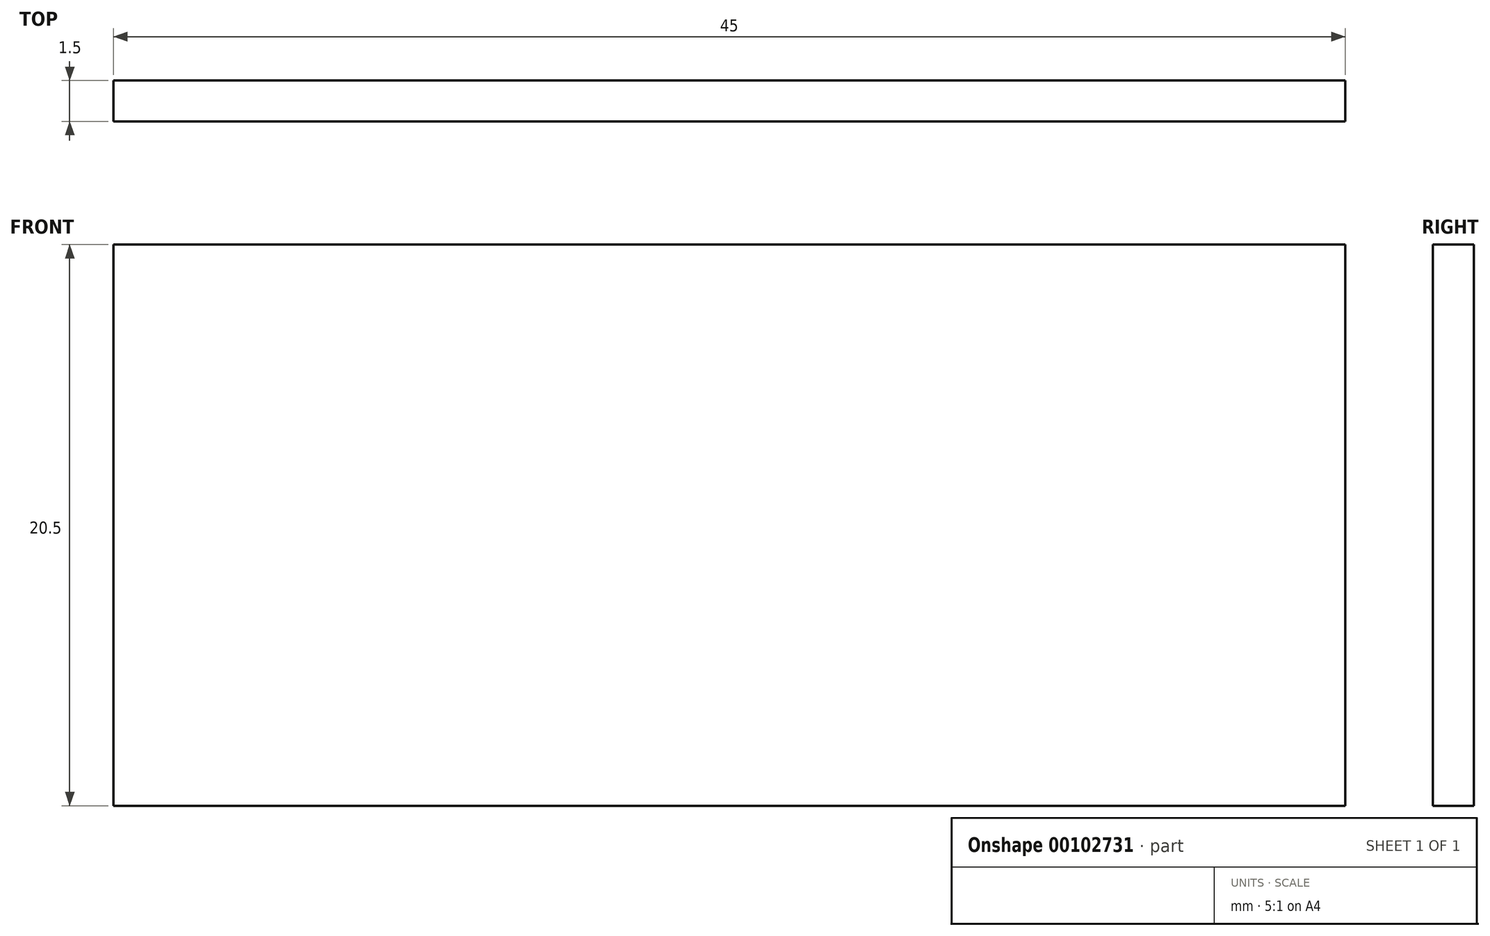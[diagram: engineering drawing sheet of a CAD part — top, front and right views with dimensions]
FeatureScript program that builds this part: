
annotation { "Feature Type Name" : "Feature", "Feature Type Description" : "" }
export const myFeature = defineFeature(function(context is Context, id is Id, definition is map)
    precondition{}
    {
        {
            var Q0;
            Q0=qCreatedBy(makeId("Front.planeOp"),FACE);
            var sketch = newSketch(context, id + "F0", { "sketchPlane" : qUnion([Q0])});
            skLineSegment(sketch, "E0.bottom", {"start": v(22.5, 10.25) * mm, "end": v(-22.5, 10.25) * mm});
            skLineSegment(sketch, "E0.top", {"start": v(22.5, -10.25) * mm, "end": v(-22.5, -10.25) * mm});
            skLineSegment(sketch, "E0.left", {"start": v(22.5, 10.25) * mm, "end": v(22.5, -10.25) * mm});
            skLineSegment(sketch, "E0.right", {"start": v(-22.5, 10.25) * mm, "end": v(-22.5, -10.25) * mm});
            skPoint(sketch, "E0.middle", {"position": v(0, 0) * mm});
            skPoint(sketch, "E1", {"position": v(-13, 0) * mm});
            skPoint(sketch, "E2", {"position": v(13, 0) * mm});
            skPoint(sketch, "E3", {"position": v(-3, -7.25) * mm});
            skPoint(sketch, "E4", {"position": v(3.25, -7.25) * mm});
            skSolve(sketch);
        }
        {
            var Q0;
            Q0=makeQuery(id+"F0.imprint","IMPRINT",FACE,{"disambiguationData":[TD([[makeQuery(id+"F0.imprint","IMPRINT",EDGE,{"derivedFrom":sQuery(id+"F0.wireOp",EDGE,"E0.bottom")}),1.0]])]});
            extrude(context, id + "F1", {"entities" : qUnion([Q0]), "depth" : 1.5 * mm});
        }
    });
